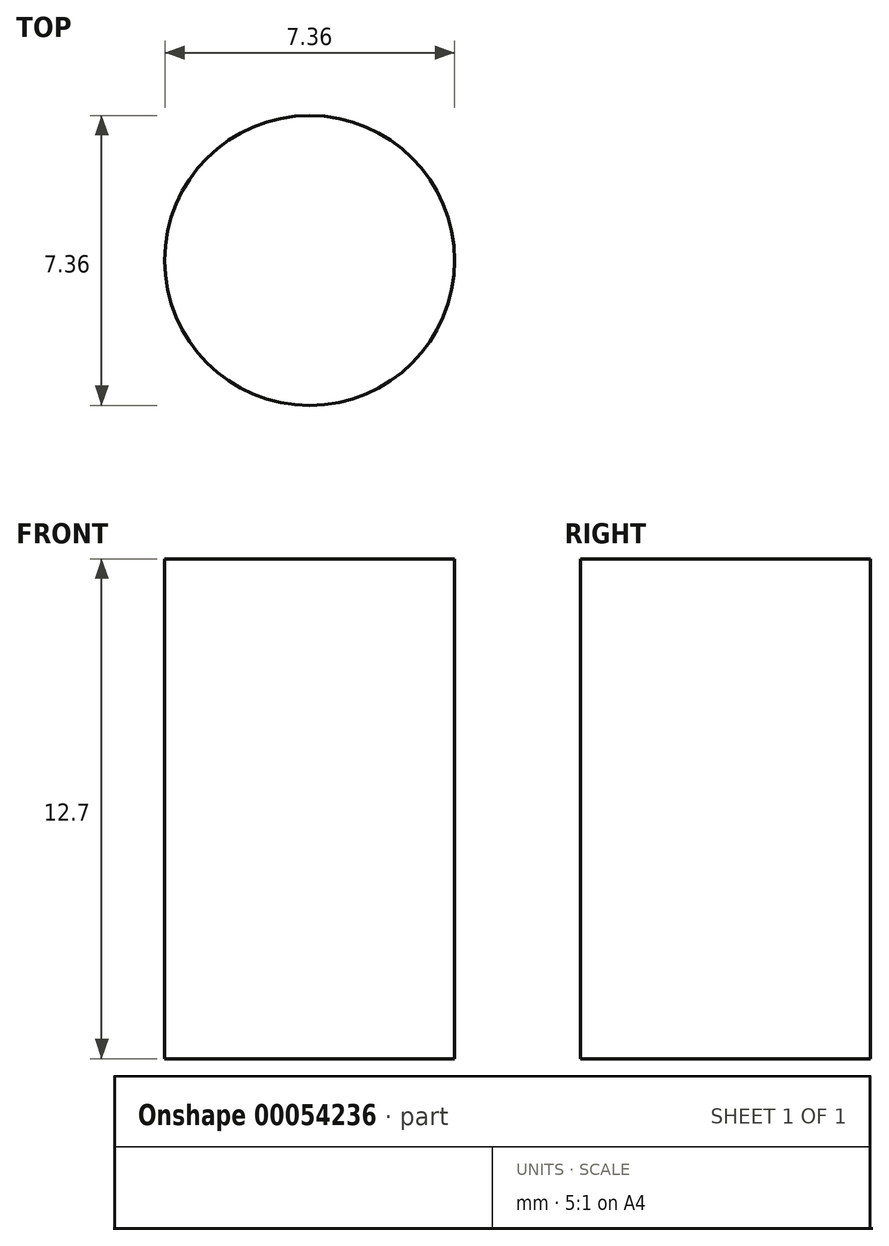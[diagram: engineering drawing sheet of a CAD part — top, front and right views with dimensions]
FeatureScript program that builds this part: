
annotation { "Feature Type Name" : "Feature", "Feature Type Description" : "" }
export const myFeature = defineFeature(function(context is Context, id is Id, definition is map)
    precondition{}
    {
        {
            var Q0;
            Q0=qCreatedBy(makeId("Top.planeOp"),FACE);
            var sketch = newSketch(context, id + "F0", { "sketchPlane" : qUnion([Q0])});
            skCircle(sketch, "E0", {"center": v(0, 0) * mm, "radius": 3.68 * mm});
            skSolve(sketch);
        }
        {
            var Q0;
            Q0 = qSketchRegion(id + "F0", true);
            extrude(context, id + "F1", {"entities" : qUnion([Q0]), "depth" : 12.7 * mm});
        }
    });
